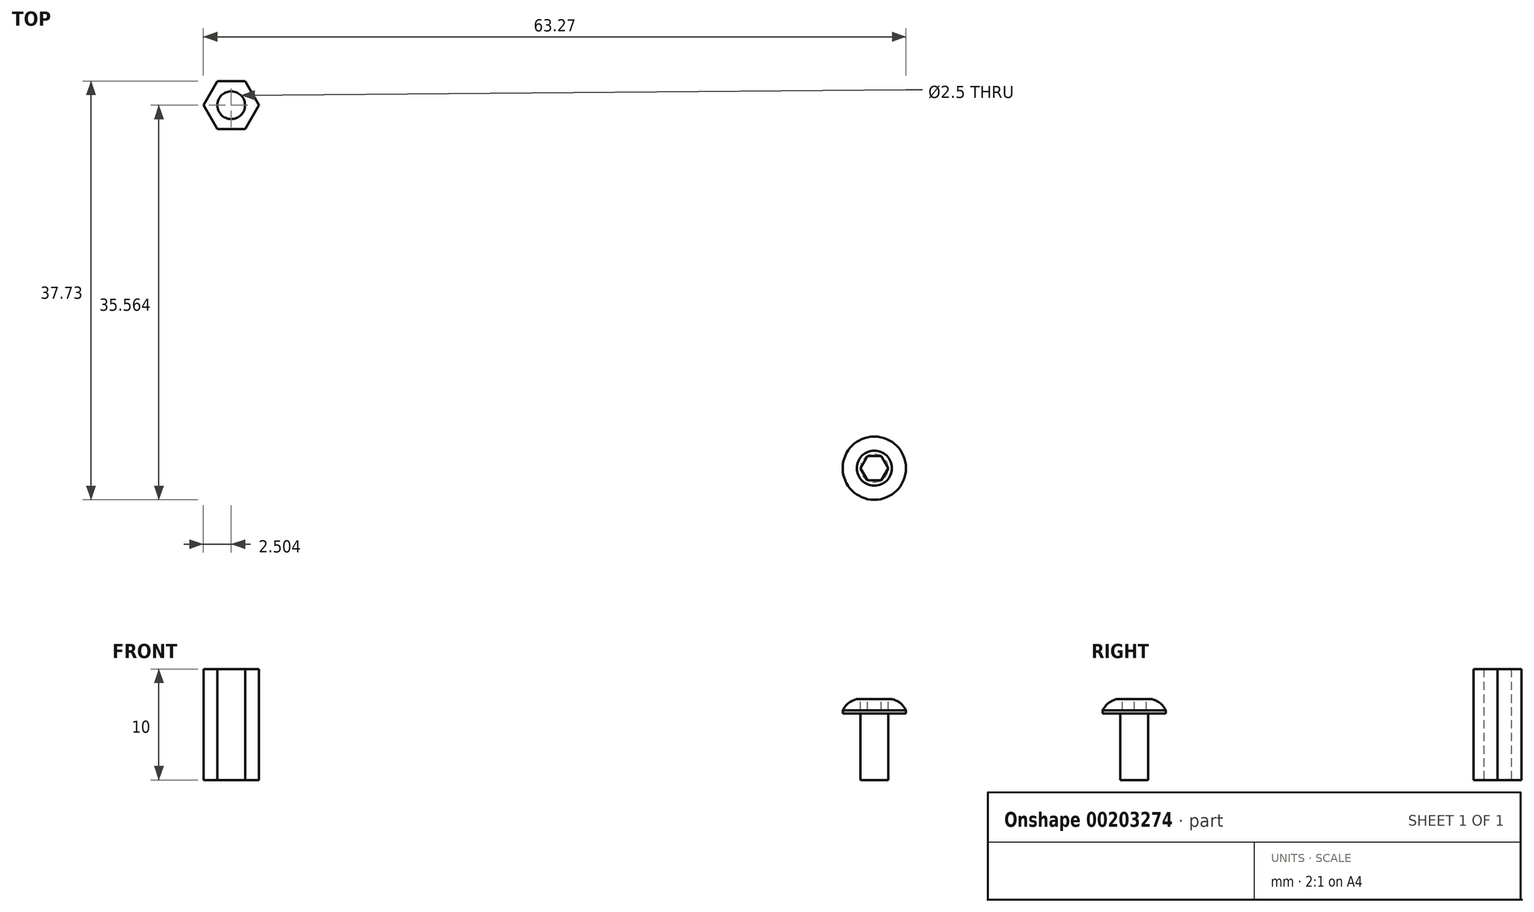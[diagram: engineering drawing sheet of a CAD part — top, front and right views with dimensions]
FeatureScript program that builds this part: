
annotation { "Feature Type Name" : "Feature", "Feature Type Description" : "" }
export const myFeature = defineFeature(function(context is Context, id is Id, definition is map)
    precondition{}
    {
        {
            var Q0;
            Q0=qCreatedBy(makeId("Front.planeOp"),FACE);
            var sketch = newSketch(context, id + "F0", { "sketchPlane" : qUnion([Q0])});
            skLineSegment(sketch, "E0", {"start": v(0, 0) * mm, "end": v(1.25, 0) * mm});
            skLineSegment(sketch, "E1", {"start": v(1.25, 0) * mm, "end": v(1.25, 6) * mm});
            skLineSegment(sketch, "E2", {"start": v(1.25, 6) * mm, "end": v(0, 6) * mm});
            skLineSegment(sketch, "E3", {"start": v(0, 6) * mm, "end": v(0, 0) * mm});
            skLineSegment(sketch, "E4", {"start": v(1.25, 6) * mm, "end": v(2.85, 6) * mm});
            skLineSegment(sketch, "E5", {"start": v(2.85, 6) * mm, "end": v(2.85, 6.28) * mm});
            skLineSegment(sketch, "E6", {"start": v(0, 6) * mm, "end": v(0, 7.3) * mm});
            skFitSpline(sketch, "E7", {"points": [v(2.85, 6.28) * mm, v(2.37, 6.9) * mm, v(1.58, 7.3) * mm], "startDerivative": vector(-0.86, 1.43) * mm, "endDerivative": vector(-1.68, 0.63) * mm});
            skLineSegment(sketch, "E8", {"start": v(0, 7.3) * mm, "end": v(1.58, 7.3) * mm});
            skSolve(sketch);
        }
        {
            var Q0;
            Q0 = qSketchRegion(id + "F0", true);
            var Q1;
            Q1=sQuery(id+"F0.wireOp",EDGE,"E3");
            revolve(context, id + "F1", {"entities" : qUnion([Q0]), "axis" : qUnion([Q1]), "revolveType" : RevolveType.FULL});
        }
        {
            var Q0;
            Q0=makeQuery(id+"F1.opRevolve","SWEPT_FACE",FACE,{"disambiguationData":[OSD([sQuery(id+"F0.wireOp",EDGE,"E8")])]});
            var sketch = newSketch(context, id + "F2", { "sketchPlane" : qUnion([Q0])});
            skCircle(sketch, "E9.cCircle", {"center": v(0, 0) * mm, "radius": 1.25 * mm, "construction": true});
            skLineSegment(sketch, "E9.0", {"start": v(1.25, 0) * mm, "end": v(0.62, -1.08) * mm});
            skLineSegment(sketch, "E9.1", {"start": v(0.63, -1.08) * mm, "end": v(-0.62, -1.08) * mm});
            skLineSegment(sketch, "E9.2", {"start": v(-0.62, -1.08) * mm, "end": v(-1.25, 0) * mm});
            skLineSegment(sketch, "E9.3", {"start": v(-1.25, 0) * mm, "end": v(-0.63, 1.08) * mm});
            skLineSegment(sketch, "E9.4", {"start": v(-0.63, 1.08) * mm, "end": v(0.62, 1.08) * mm});
            skLineSegment(sketch, "E9.5", {"start": v(0.62, 1.08) * mm, "end": v(1.25, 0) * mm});
            skLineSegment(sketch, "E10", {"start": v(-1.25, 0) * mm, "end": v(1.25, 0) * mm});
            skSolve(sketch);
        }
        {
            var Q0;
            Q0 = qSketchRegion(id + "F2", true);
            extrude(context, id + "F3", {"entities" : qUnion([Q0]), "operationType" : NewBodyOperationType.REMOVE, "oppositeDirection" : true, "depth" : 1 * mm});
        }
        {
            var Q0;
            Q0=qCreatedBy(makeId("Top.planeOp"),FACE);
            var sketch = newSketch(context, id + "F4", { "sketchPlane" : qUnion([Q0])});
            skCircle(sketch, "E11.cCircle", {"center": v(-57.92, 32.71) * mm, "radius": 2.5 * mm, "construction": true});
            skLineSegment(sketch, "E11.0", {"start": v(-55.42, 32.71) * mm, "end": v(-56.67, 30.55) * mm});
            skLineSegment(sketch, "E11.1", {"start": v(-56.67, 30.55) * mm, "end": v(-59.17, 30.55) * mm});
            skLineSegment(sketch, "E11.2", {"start": v(-59.17, 30.55) * mm, "end": v(-60.42, 32.71) * mm});
            skLineSegment(sketch, "E11.3", {"start": v(-60.42, 32.71) * mm, "end": v(-59.17, 34.88) * mm});
            skLineSegment(sketch, "E11.4", {"start": v(-59.17, 34.88) * mm, "end": v(-56.67, 34.88) * mm});
            skLineSegment(sketch, "E11.5", {"start": v(-56.67, 34.88) * mm, "end": v(-55.42, 32.71) * mm});
            skLineSegment(sketch, "E12", {"start": v(-57.92, 32.71) * mm, "end": v(-57.92, 30.55) * mm, "construction": true});
            skCircle(sketch, "E13", {"center": v(-57.92, 32.71) * mm, "radius": 1.25 * mm});
            skSolve(sketch);
        }
        {
            var Q0;
            Q0 = qSketchRegion(id + "F4", true);
            extrude(context, id + "F5", {"entities" : qUnion([Q0]), "depth" : 10 * mm});
        }
    });
